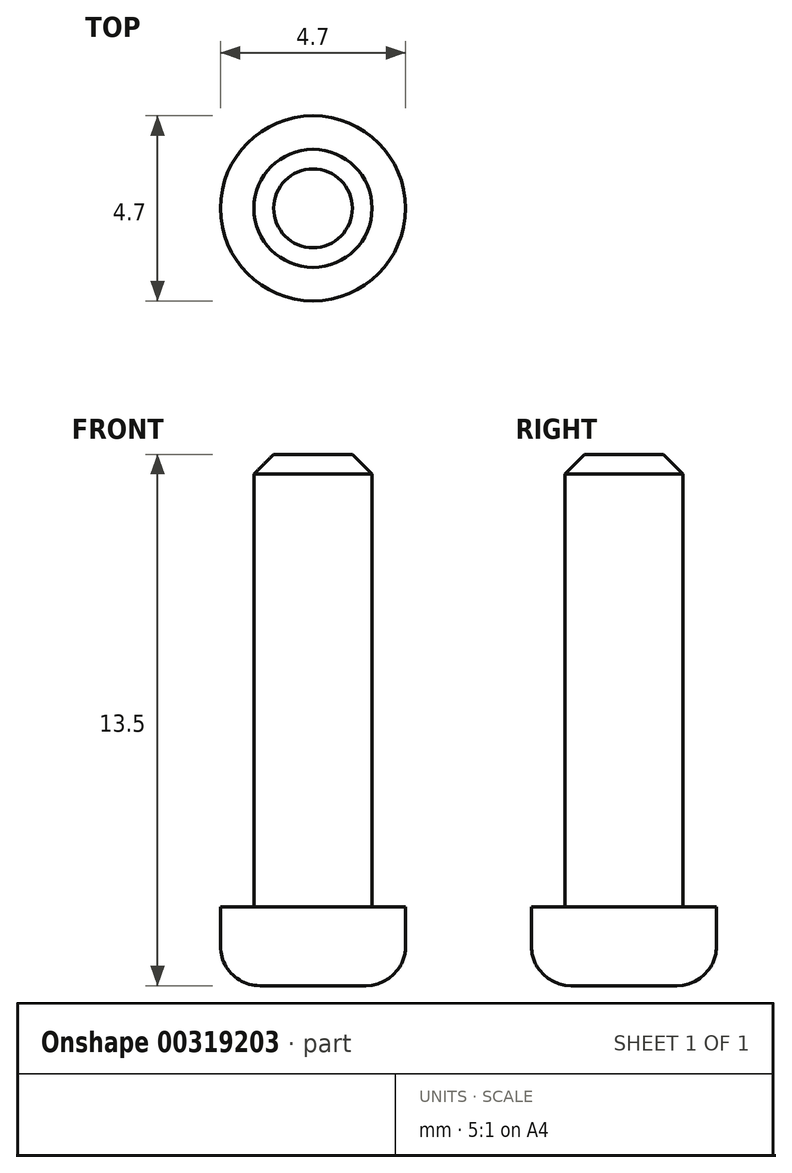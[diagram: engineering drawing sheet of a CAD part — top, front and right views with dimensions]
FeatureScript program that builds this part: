
annotation { "Feature Type Name" : "Feature", "Feature Type Description" : "" }
export const myFeature = defineFeature(function(context is Context, id is Id, definition is map)
    precondition{}
    {
        {
            var Q0;
            Q0=qCreatedBy(makeId("Front.planeOp"),FACE);
            var sketch = newSketch(context, id + "F0", { "sketchPlane" : qUnion([Q0])});
            skLineSegment(sketch, "E0", {"start": v(-1.5, 13.5) * mm, "end": v(-1.5, 2) * mm});
            skLineSegment(sketch, "E1", {"start": v(-1.5, 2) * mm, "end": v(-2.35, 2) * mm});
            skLineSegment(sketch, "E2", {"start": v(-2.35, 2) * mm, "end": v(-2.35, 0) * mm});
            skLineSegment(sketch, "E3", {"start": v(-2.35, 0) * mm, "end": v(0, 0) * mm});
            skLineSegment(sketch, "E4", {"start": v(-1.5, 13.5) * mm, "end": v(0, 13.5) * mm});
            skLineSegment(sketch, "E5", {"start": v(0, 60.6) * mm, "end": v(0, -53.96) * mm, "construction": true});
            skLineSegment(sketch, "E6", {"start": v(0, 13.5) * mm, "end": v(0, 0) * mm});
            skSolve(sketch);
        }
        {
            var Q0;
            Q0 = qSketchRegion(id + "F0", true);
            var Q1;
            Q1=sQuery(id+"F0.wireOp",EDGE,"E5");
            revolve(context, id + "F1", {"surfaceOperationType" : NewSurfaceOperationType.NEW, "entities" : qUnion([Q0]), "axis" : qUnion([Q1]), "revolveType" : RevolveType.FULL});
        }
        {
            var Q0;
            Q0=makeQuery(id+"F1.opRevolve","SWEPT_EDGE",EDGE,{"disambiguationData":[OSD([sQuery(id+"F0.wireOp",EDGE,"E0"),sQuery(id+"F0.wireOp",EDGE,"E4")])]});
            chamfer(context, id + "F2", {"entities" : qUnion([Q0]), "width" : .5 * mm, "tangentPropagation" : true});
        }
        {
            var Q0;
            Q0=makeQuery(id+"F1.opRevolve","SWEPT_EDGE",EDGE,{"disambiguationData":[OSD([sQuery(id+"F0.wireOp",EDGE,"E2"),sQuery(id+"F0.wireOp",EDGE,"E3")])]});
            fillet(context, id + "F3", {"entities" : qUnion([Q0]), "radius" : 1 * mm, "tangentPropagation" : true, "allowEdgeOverflow" : false});
        }
    });
